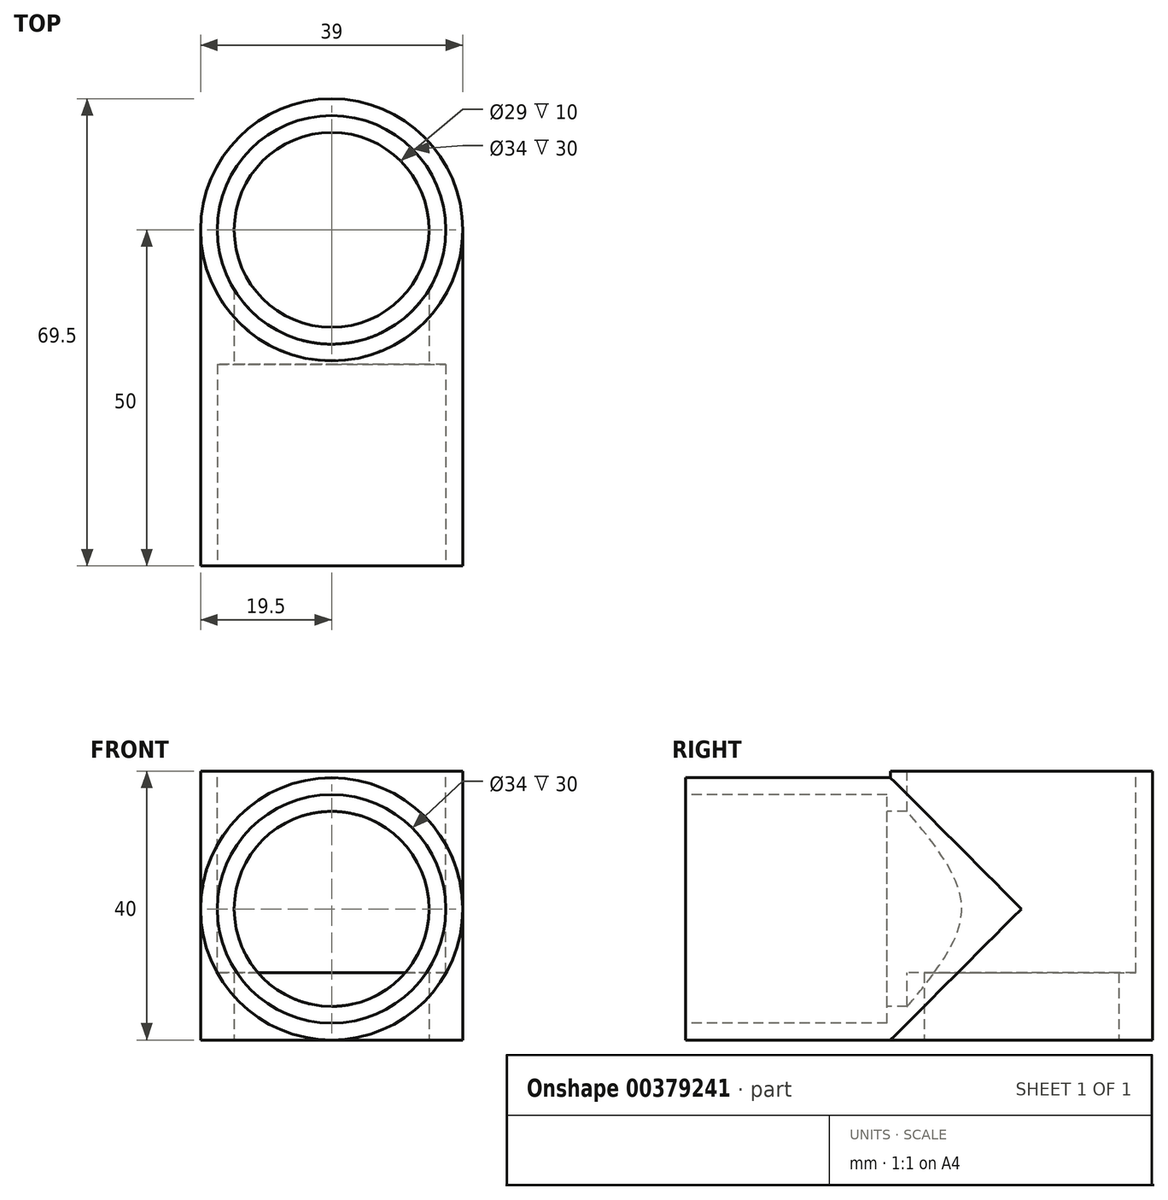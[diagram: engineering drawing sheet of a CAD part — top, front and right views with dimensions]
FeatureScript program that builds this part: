
annotation { "Feature Type Name" : "Feature", "Feature Type Description" : "" }
export const myFeature = defineFeature(function(context is Context, id is Id, definition is map)
    precondition{}
    {
        {
            var Q0;
            Q0=qCreatedBy(makeId("Top.planeOp"),FACE);
            var sketch = newSketch(context, id + "F0", { "sketchPlane" : qUnion([Q0])});
            skCircle(sketch, "E0", {"center": v(0, 0) * mm, "radius": 17 * mm, "construction": true});
            skCircle(sketch, "E1", {"center": v(0, 0) * mm, "radius": 19.5 * mm});
            skCircle(sketch, "E2", {"center": v(0, 0) * mm, "radius": 14.5 * mm});
            skSolve(sketch);
        }
        {
            var Q0;
            Q0 = qSketchRegion(id + "F0", true);
            extrude(context, id + "F1", {"entities" : qUnion([Q0]), "depth" : 40 * mm});
        }
        {
            var Q0;
            Q0=makeQuery(id+"F1.opExtrude","CAP_FACE",FACE,{"disambiguationData":[OSD([sQuery(id+"F0.wireOp",EDGE,"E1"),sQuery(id+"F0.wireOp",EDGE,"E2")])],"isStart":false});
            var sketch = newSketch(context, id + "F2", { "sketchPlane" : qUnion([Q0])});
            skCircle(sketch, "E3", {"center": v(0, 0) * mm, "radius": 17 * mm});
            skSolve(sketch);
        }
        {
            var Q0;
            Q0 = qSketchRegion(id + "F2", true);
            extrude(context, id + "F3", {"entities" : qUnion([Q0]), "operationType" : NewBodyOperationType.REMOVE, "oppositeDirection" : true, "depth" : 30 * mm});
        }
        {
            var Q0;
            Q0=qCreatedBy(makeId("Front.planeOp"),FACE);
            cPlane(context, id + "F4", {"entities" : qUnion([Q0]), "cplaneType" : CPlaneType.OFFSET, "offset" : 50 * mm, "width" : 150 * mm, "height" : 150 * mm});
        }
        {
            var Q0;
            Q0=qCreatedBy(id+"F4.planeOp",FACE);
            var sketch = newSketch(context, id + "F5", { "sketchPlane" : qUnion([Q0])});
            skCircle(sketch, "E4", {"center": v(0, 19.5) * mm, "radius": 19.5 * mm});
            skCircle(sketch, "E5", {"center": v(0, 19.5) * mm, "radius": 17 * mm, "construction": true});
            skSolve(sketch);
        }
        {
            var Q0;
            Q0=makeQuery(id+"F5.imprint","IMPRINT",FACE,{"disambiguationData":[TD([[makeQuery(id+"F5.imprint","IMPRINT",EDGE,{"derivedFrom":sQuery(id+"F5.wireOp",EDGE,"E4")}),1.0]])]});
            extrude(context, id + "F6", {"entities" : qUnion([Q0]), "operationType" : NewBodyOperationType.ADD, "endBound" : BoundingType.UP_TO_NEXT, "oppositeDirection" : true, "depth" : 25 * mm});
        }
        {
            var Q0;
            Q0=qCreatedBy(id+"F4.planeOp",FACE);
            var sketch = newSketch(context, id + "F7", { "sketchPlane" : qUnion([Q0])});
            skCircle(sketch, "E6", {"center": v(0, 19.5) * mm, "radius": 14.5 * mm});
            skSolve(sketch);
        }
        {
            var Q0;
            Q0 = qSketchRegion(id + "F7", true);
            var Q1;
            Q1=makeQuery(id+"F3.boolean.opBoolean","COPY",FACE,{"derivedFrom":makeQuery(id+"F3.opExtrude","SWEPT_FACE",FACE,{"disambiguationData":[OSD([sQuery(id+"F2.wireOp",EDGE,"E3")])]})});
            extrude(context, id + "F8", {"entities" : qUnion([Q0]), "operationType" : NewBodyOperationType.REMOVE, "endBound" : BoundingType.UP_TO_SURFACE, "oppositeDirection" : true, "endBoundEntityFace" : qUnion([Q1]), "depth" : 25 * mm});
        }
        {
            var Q0;
            Q0=qCreatedBy(id+"F4.planeOp",FACE);
            var sketch = newSketch(context, id + "F9", { "sketchPlane" : qUnion([Q0])});
            skCircle(sketch, "E7", {"center": v(0, 19.5) * mm, "radius": 17 * mm});
            skSolve(sketch);
        }
        {
            var Q0;
            Q0 = qSketchRegion(id + "F9", true);
            extrude(context, id + "F10", {"entities" : qUnion([Q0]), "operationType" : NewBodyOperationType.REMOVE, "oppositeDirection" : true, "depth" : 30 * mm});
        }
    });
